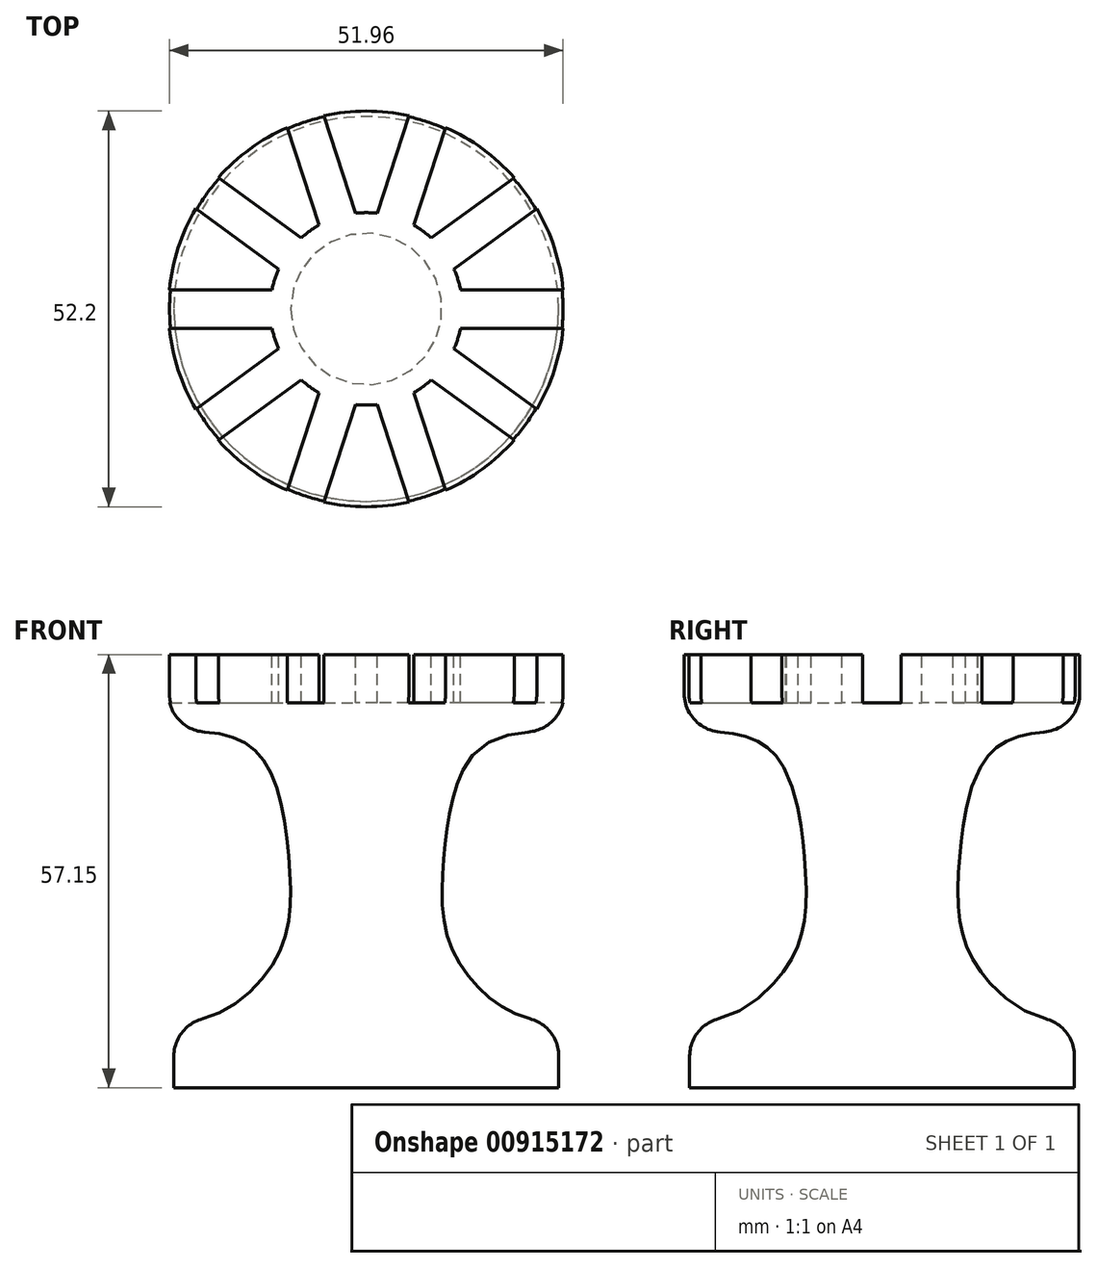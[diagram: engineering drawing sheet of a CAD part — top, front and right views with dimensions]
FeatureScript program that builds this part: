
annotation { "Feature Type Name" : "Feature", "Feature Type Description" : "" }
export const myFeature = defineFeature(function(context is Context, id is Id, definition is map)
    precondition{}
    {
        {
            var Q0;
            Q0=qCreatedBy(makeId("Front.planeOp"),FACE);
            var sketch = newSketch(context, id + "F0", { "sketchPlane" : qUnion([Q0])});
            skLineSegment(sketch, "E0", {"start": v(0, 0) * mm, "end": v(0, 57.15) * mm});
            skLineSegment(sketch, "E1", {"start": v(0, 0) * mm, "end": v(25.4, 0) * mm});
            skLineSegment(sketch, "E2", {"start": v(25.4, 0) * mm, "end": v(25.4, 8.9) * mm});
            skLineSegment(sketch, "E3", {"start": v(0, 47) * mm, "end": v(26.1, 47) * mm, "construction": true});
            skFitSpline(sketch, "E4", {"points": [v(25.4, 8.9) * mm, v(12.16, 16.6) * mm, v(10.2, 29.75) * mm, v(13.8, 43.56) * mm, v(23.12, 47) * mm], "startDerivative": vector(-59.37, -9.33) * mm, "endDerivative": vector(55.95, 0) * mm});
            skLineSegment(sketch, "E5.bottom", {"start": v(0, 57.15) * mm, "end": v(26.1, 57.15) * mm});
            skLineSegment(sketch, "E5.top", {"start": v(0, 47) * mm, "end": v(26.1, 47) * mm});
            skLineSegment(sketch, "E5.left", {"start": v(0, 57.15) * mm, "end": v(0, 47) * mm});
            skLineSegment(sketch, "E5.right", {"start": v(26.1, 57.15) * mm, "end": v(26.1, 47) * mm});
            skSolve(sketch);
        }
        {
            var Q0;
            {var subQ1=sQuery(id+"F0.wireOp",EDGE,"E0");Q0=makeQuery(id+"F0.imprint","IMPRINT",FACE,{"disambiguationData":[TD([[makeQuery(id+"F0.imprint","IMPRINT",EDGE,{"derivedFrom":subQ1}),-1.0]])]});}
            var Q1;
            Q1=makeQuery(id+"F0.imprint","IMPRINT",FACE,{"disambiguationData":[TD([[makeQuery(id+"F0.imprint","IMPRINT",EDGE,{"derivedFrom":sQuery(id+"F0.wireOp",EDGE,"E5.bottom")}),-1.0]])]});
            var Q2;
            Q2=sQuery(id+"F0.wireOp",EDGE,"E0");
            revolve(context, id + "F1", {"surfaceOperationType" : NewSurfaceOperationType.NEW, "entities" : qUnion([Q0, Q1]), "axis" : qUnion([Q2]), "revolveType" : RevolveType.FULL});
        }
        {
            var Q0;
            Q0=makeQuery(id+"F1.opRevolve","SWEPT_FACE",FACE,{"disambiguationData":[OSD([sQuery(id+"F0.wireOp",EDGE,"E5.bottom")])]});
            var sketch = newSketch(context, id + "F2", { "sketchPlane" : qUnion([Q0])});
            skCircle(sketch, "E6", {"center": v(0, 0) * mm, "radius": 12.7 * mm});
            skSolve(sketch);
        }
        {
            var Q0;
            Q0=makeQuery(id+"F2.imprint","IMPRINT",FACE,{"disambiguationData":[TD([[makeQuery(id+"F2.imprint","IMPRINT",EDGE,{"derivedFrom":sQuery(id+"F2.wireOp",EDGE,"E6")}),1.0]])]});
            extrude(context, id + "F3", {"entities" : qUnion([Q0]), "operationType" : NewBodyOperationType.REMOVE, "oppositeDirection" : true, "depth" : 6.35 * mm, "offsetDistance" : 25.4 * mm});
        }
        {
            var Q0;
            Q0=makeQuery(id+"F1.opRevolve","SWEPT_FACE",FACE,{"disambiguationData":[OSD([sQuery(id+"F0.wireOp",EDGE,"E5.bottom")])]});
            var sketch = newSketch(context, id + "F4", { "sketchPlane" : qUnion([Q0])});
            skLineSegment(sketch, "E7", {"start": v(0, 0) * mm, "end": v(19.05, 0) * mm, "construction": true});
            skLineSegment(sketch, "E8.bottom", {"start": v(28.01, -2.54) * mm, "end": v(10.09, -2.54) * mm});
            skLineSegment(sketch, "E8.top", {"start": v(28.01, 2.54) * mm, "end": v(10.09, 2.54) * mm});
            skLineSegment(sketch, "E8.left", {"start": v(28.01, -2.54) * mm, "end": v(28.01, 2.54) * mm});
            skLineSegment(sketch, "E8.right", {"start": v(10.09, -2.54) * mm, "end": v(10.09, 2.54) * mm});
            skPoint(sketch, "E8.middle", {"position": v(19.05, 0) * mm});
            skLineSegment(sketch, "E9.1.0", {"start": v(9.65, 3.87) * mm, "end": v(6.67, 7.98) * mm});
            skPoint(sketch, "E9.1.1", {"position": v(15.41, 11.2) * mm});
            skLineSegment(sketch, "E9.1.2", {"start": v(24.16, 14.41) * mm, "end": v(21.17, 18.52) * mm});
            skLineSegment(sketch, "E9.1.3", {"start": v(24.16, 14.41) * mm, "end": v(9.65, 3.87) * mm});
            skLineSegment(sketch, "E9.1.4", {"start": v(21.17, 18.52) * mm, "end": v(6.67, 7.98) * mm});
            skLineSegment(sketch, "E9.2.0", {"start": v(5.53, 8.8) * mm, "end": v(0.7, 10.38) * mm});
            skPoint(sketch, "E9.2.1", {"position": v(5.89, 18.12) * mm});
            skLineSegment(sketch, "E9.2.2", {"start": v(11.07, 25.86) * mm, "end": v(6.24, 27.43) * mm});
            skLineSegment(sketch, "E9.2.3", {"start": v(11.07, 25.86) * mm, "end": v(5.53, 8.8) * mm});
            skLineSegment(sketch, "E9.2.4", {"start": v(6.24, 27.43) * mm, "end": v(0.7, 10.38) * mm});
            skLineSegment(sketch, "E9.3.0", {"start": v(-0.7, 10.38) * mm, "end": v(-5.53, 8.8) * mm});
            skPoint(sketch, "E9.3.1", {"position": v(-5.89, 18.12) * mm});
            skLineSegment(sketch, "E9.3.2", {"start": v(-6.24, 27.43) * mm, "end": v(-11.07, 25.86) * mm});
            skLineSegment(sketch, "E9.3.3", {"start": v(-6.24, 27.43) * mm, "end": v(-0.7, 10.38) * mm});
            skLineSegment(sketch, "E9.3.4", {"start": v(-11.07, 25.86) * mm, "end": v(-5.53, 8.8) * mm});
            skLineSegment(sketch, "E9.4.0", {"start": v(-6.67, 7.98) * mm, "end": v(-9.65, 3.87) * mm});
            skPoint(sketch, "E9.4.1", {"position": v(-15.41, 11.2) * mm});
            skLineSegment(sketch, "E9.4.2", {"start": v(-21.17, 18.52) * mm, "end": v(-24.16, 14.41) * mm});
            skLineSegment(sketch, "E9.4.3", {"start": v(-21.17, 18.52) * mm, "end": v(-6.67, 7.98) * mm});
            skLineSegment(sketch, "E9.4.4", {"start": v(-24.16, 14.41) * mm, "end": v(-9.65, 3.87) * mm});
            skLineSegment(sketch, "E9.5.0", {"start": v(-10.09, 2.54) * mm, "end": v(-10.09, -2.54) * mm});
            skPoint(sketch, "E9.5.1", {"position": v(-19.05, 0) * mm});
            skLineSegment(sketch, "E9.5.2", {"start": v(-28.01, 2.54) * mm, "end": v(-28.01, -2.54) * mm});
            skLineSegment(sketch, "E9.5.3", {"start": v(-28.01, 2.54) * mm, "end": v(-10.09, 2.54) * mm});
            skLineSegment(sketch, "E9.5.4", {"start": v(-28.01, -2.54) * mm, "end": v(-10.09, -2.54) * mm});
            skLineSegment(sketch, "E9.6.0", {"start": v(-9.65, -3.87) * mm, "end": v(-6.67, -7.98) * mm});
            skPoint(sketch, "E9.6.1", {"position": v(-15.41, -11.2) * mm});
            skLineSegment(sketch, "E9.6.2", {"start": v(-24.16, -14.41) * mm, "end": v(-21.17, -18.52) * mm});
            skLineSegment(sketch, "E9.6.3", {"start": v(-24.16, -14.41) * mm, "end": v(-9.65, -3.87) * mm});
            skLineSegment(sketch, "E9.6.4", {"start": v(-21.17, -18.52) * mm, "end": v(-6.67, -7.98) * mm});
            skLineSegment(sketch, "E9.7.0", {"start": v(-5.53, -8.8) * mm, "end": v(-0.7, -10.38) * mm});
            skPoint(sketch, "E9.7.1", {"position": v(-5.89, -18.12) * mm});
            skLineSegment(sketch, "E9.7.2", {"start": v(-11.07, -25.86) * mm, "end": v(-6.24, -27.43) * mm});
            skLineSegment(sketch, "E9.7.3", {"start": v(-11.07, -25.86) * mm, "end": v(-5.53, -8.8) * mm});
            skLineSegment(sketch, "E9.7.4", {"start": v(-6.24, -27.43) * mm, "end": v(-0.7, -10.38) * mm});
            skLineSegment(sketch, "E9.8.0", {"start": v(0.7, -10.38) * mm, "end": v(5.53, -8.8) * mm});
            skPoint(sketch, "E9.8.1", {"position": v(5.89, -18.12) * mm});
            skLineSegment(sketch, "E9.8.2", {"start": v(6.24, -27.43) * mm, "end": v(11.07, -25.86) * mm});
            skLineSegment(sketch, "E9.8.3", {"start": v(6.24, -27.43) * mm, "end": v(0.7, -10.38) * mm});
            skLineSegment(sketch, "E9.8.4", {"start": v(11.07, -25.86) * mm, "end": v(5.53, -8.8) * mm});
            skLineSegment(sketch, "E9.9.0", {"start": v(6.67, -7.98) * mm, "end": v(9.65, -3.87) * mm});
            skPoint(sketch, "E9.9.1", {"position": v(15.41, -11.2) * mm});
            skLineSegment(sketch, "E9.9.2", {"start": v(21.17, -18.52) * mm, "end": v(24.16, -14.41) * mm});
            skLineSegment(sketch, "E9.9.3", {"start": v(21.17, -18.52) * mm, "end": v(6.67, -7.98) * mm});
            skLineSegment(sketch, "E9.9.4", {"start": v(24.16, -14.41) * mm, "end": v(9.65, -3.87) * mm});
            skPoint(sketch, "E9.center", {"position": v(0, 0) * mm});
            skSolve(sketch);
        }
        {
            var Q0;
            Q0 = qSketchRegion(id + "F4", true);
            extrude(context, id + "F5", {"entities" : qUnion([Q0]), "operationType" : NewBodyOperationType.REMOVE, "oppositeDirection" : true, "depth" : 6.35 * mm, "offsetDistance" : 25.4 * mm});
        }
        {
            var Q0;
            Q0=makeQuery(id+"F1.opRevolve","SWEPT_EDGE",EDGE,{"disambiguationData":[OSD([sQuery(id+"F0.wireOp",EDGE,"E2"),sQuery(id+"F0.wireOp",EDGE,"E4")])]});
            var Q1;
            Q1=makeQuery(id+"F1.opRevolve","SWEPT_EDGE",EDGE,{"disambiguationData":[OSD([sQuery(id+"F0.wireOp",EDGE,"E5.top"),sQuery(id+"F0.wireOp",EDGE,"E5.right")])]});
            fillet(context, id + "F6", {"entities" : qUnion([Q0, Q1]), "radius" : 5.08 * mm, "tangentPropagation" : true, "allowEdgeOverflow" : false});
        }
    });
